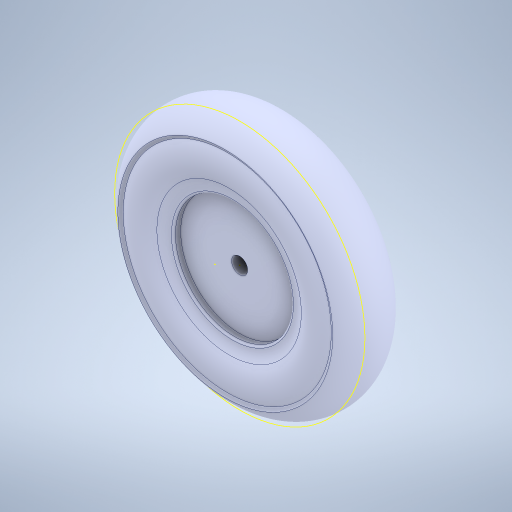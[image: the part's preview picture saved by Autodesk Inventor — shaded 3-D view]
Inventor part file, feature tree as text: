
AUTODESK INVENTOR PART (.ipt)
format: ipt  version: 2023 (Build 270158000, 158)  size: 682,496 bytes
history: native  units: in
note: dims shown in document units (in); Inventor stores cm internally (conversion verified against a paired STEP export)
features: sketch x2, extrude x1, projected_geometry x1, other x1
ambient origin geometry x8: Origin, YZ Plane, XZ Plane, XY Plane, X Axis, Y Axis, Z Axis, Center Point
bodies: Solid5 (feature_tree)
feature tree (5):
  extrude  "Extrusion2"  Depth=0.3937in TaperAngle=0.0deg
  sketch  "Sketch3"
  sketch  "Sketch2"  dims[d4=0.5in d5=0.3937in d6=0.0in]
  projected_geometry  "Projected Loop1"
  other  "Tire_5:1"
